# Revit family: 292 BFS-LAM-DSD-PL-___ (LOD400)
name_source: partatom
category: Fire Alarm Devices
revit_build: Autodesk Revit 2018 (Build: 20170223_1515(x64)
units: mm (PartAtom-declared; Revit-internal decimal feet)

## family parameters
Cut with Voids When Loaded = No
Host = Face
Maintain Annotation Orientation = No
OmniClass Number = 23.29.31.17.11
OmniClass Title = Visible Fire Notification Device Lights
Part Type = Normal
Room Calculation Point = No
Round Connector Dimension = Use Diameter
Shared = No

## types (1)
- 292 BFS-LAM-DSD-PL-___ (LOD400)
    DSD.BFS.Height = 0 mm  [stored 0 ft]
    DSD.BFS.Length = 0 mm  [stored 0 ft]
    DSD.BFS.Width = 0 mm  [stored 0 ft]
    Default Elevation = 0 mm  [stored 0 ft]
    Length = 126 mm  [stored 0.413386 ft]
    Light Material = PL_Red_255-000-000
    Text Material = PL_Red_255-000-000
    Top Material = PL_White_255-255-255
    Width = 85 mm  [stored 0.278871 ft]

note: [stored X ft] marks values corroborated as IEEE doubles in the binary element streams (Revit-internal decimal feet)

## geometry (parser evidence)
native form markers: Sweep x5
no freeform markers — native parametric forms only
